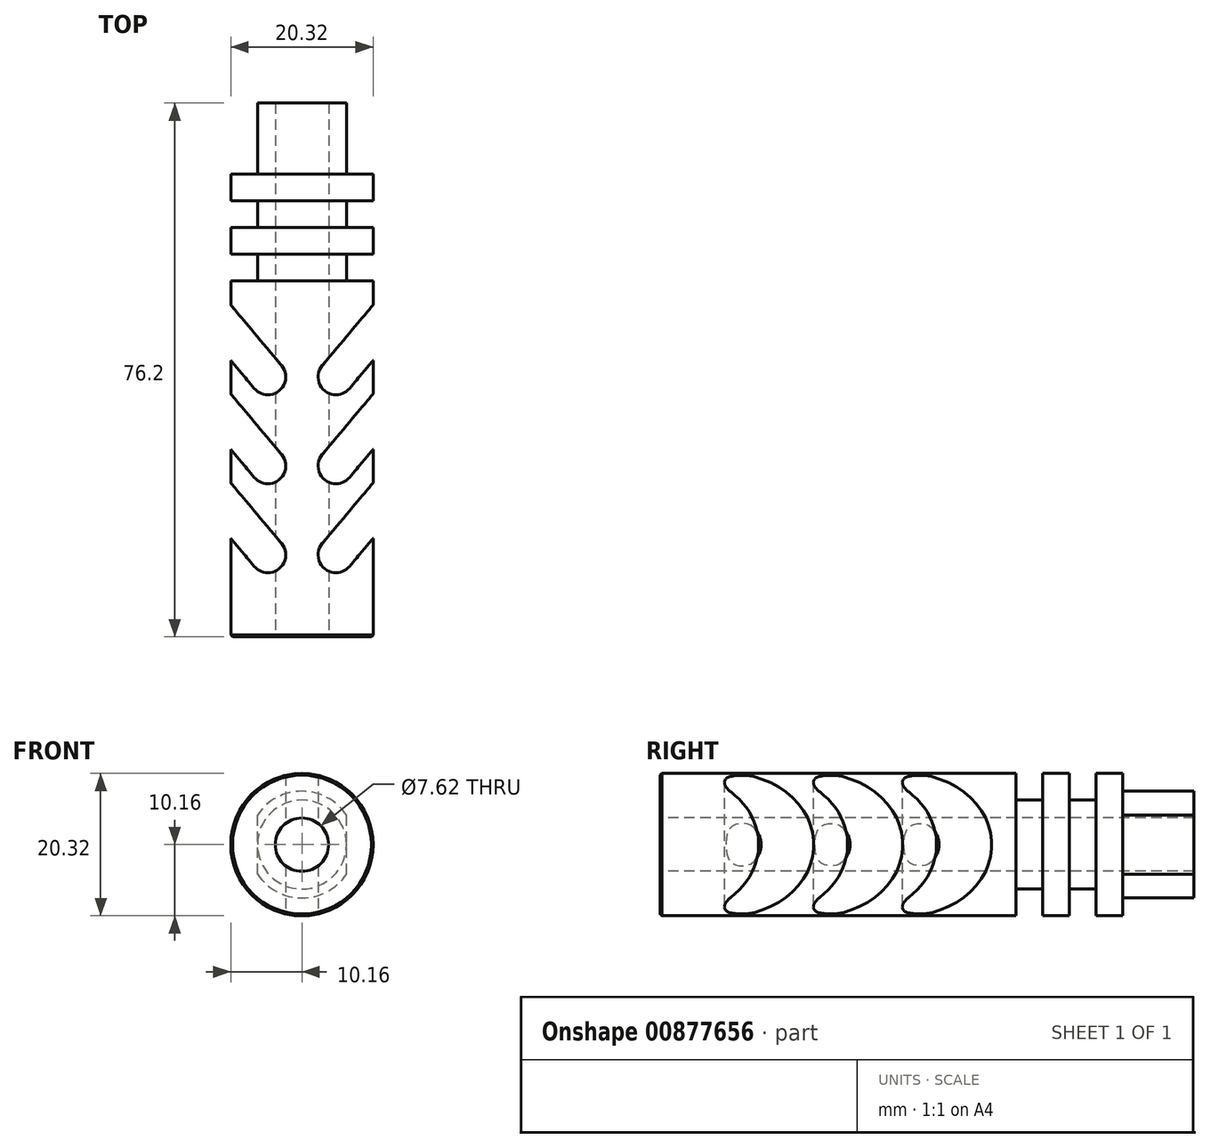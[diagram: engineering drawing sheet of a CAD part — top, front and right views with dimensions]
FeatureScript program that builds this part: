
annotation { "Feature Type Name" : "Feature", "Feature Type Description" : "" }
export const myFeature = defineFeature(function(context is Context, id is Id, definition is map)
    precondition{}
    {
        {
            var Q0;
            Q0=qCreatedBy(makeId("Front.planeOp"),FACE);
            var sketch = newSketch(context, id + "F0", { "sketchPlane" : qUnion([Q0])});
            skCircle(sketch, "E0", {"center": v(0, 0) * mm, "radius": 10.16 * mm});
            skSolve(sketch);
        }
        {
            var Q0;
            Q0=makeQuery(id+"F0.imprint","IMPRINT",FACE,{"disambiguationData":[TD([[makeQuery(id+"F0.imprint","IMPRINT",EDGE,{"derivedFrom":sQuery(id+"F0.wireOp",EDGE,"E0")}),1.0]])]});
            extrude(context, id + "F1", {"entities" : qUnion([Q0]), "oppositeDirection" : true, "depth" : 50.8 * mm, "offsetDistance" : 25.4 * mm});
        }
        {
            var Q0;
            Q0=makeQuery(id+"F1.opExtrude","CAP_FACE",FACE,{"disambiguationData":[OSD([sQuery(id+"F0.wireOp",EDGE,"E0")])],"isStart":false});
            var sketch = newSketch(context, id + "F2", { "sketchPlane" : qUnion([Q0])});
            skCircle(sketch, "E1", {"center": v(0, 0) * mm, "radius": 6.35 * mm});
            skSolve(sketch);
        }
        {
            var Q0;
            Q0=makeQuery(id+"F2.imprint","IMPRINT",FACE,{"disambiguationData":[TD([[makeQuery(id+"F2.imprint","IMPRINT",EDGE,{"derivedFrom":sQuery(id+"F2.wireOp",EDGE,"E1")}),1.0]])]});
            extrude(context, id + "F3", {"entities" : qUnion([Q0]), "operationType" : NewBodyOperationType.ADD, "depth" : 3.8 * mm, "offsetDistance" : 25.4 * mm});
        }
        {
            var Q0;
            Q0=makeQuery(id+"F3.opExtrude","CAP_FACE",FACE,{"disambiguationData":[OSD([sQuery(id+"F2.wireOp",EDGE,"E1")])],"isStart":false});
            var sketch = newSketch(context, id + "F4", { "sketchPlane" : qUnion([Q0])});
            skCircle(sketch, "E2", {"center": v(0, 0) * mm, "radius": 10.16 * mm});
            skSolve(sketch);
        }
        {
            var Q0;
            Q0 = qSketchRegion(id + "F4", true);
            extrude(context, id + "F5", {"entities" : qUnion([Q0]), "operationType" : NewBodyOperationType.ADD, "depth" : 3.8 * mm, "offsetDistance" : 25.4 * mm});
        }
        {
            var Q0;
            Q0=makeQuery(id+"F5.opExtrude","CAP_FACE",FACE,{"disambiguationData":[OSD([sQuery(id+"F4.wireOp",EDGE,"E2")])],"isStart":false});
            var sketch = newSketch(context, id + "F6", { "sketchPlane" : qUnion([Q0])});
            skCircle(sketch, "E3", {"center": v(0, 0) * mm, "radius": 6.35 * mm});
            skSolve(sketch);
        }
        {
            var Q0;
            Q0=makeQuery(id+"F6.imprint","IMPRINT",FACE,{"disambiguationData":[TD([[makeQuery(id+"F6.imprint","IMPRINT",EDGE,{"derivedFrom":sQuery(id+"F6.wireOp",EDGE,"E3")}),1.0]])]});
            extrude(context, id + "F7", {"entities" : qUnion([Q0]), "operationType" : NewBodyOperationType.ADD, "depth" : 3.8 * mm, "offsetDistance" : 25.4 * mm});
        }
        {
            var Q0;
            Q0=makeQuery(id+"F7.opExtrude","CAP_FACE",FACE,{"disambiguationData":[OSD([sQuery(id+"F6.wireOp",EDGE,"E3")])],"isStart":false});
            var sketch = newSketch(context, id + "F8", { "sketchPlane" : qUnion([Q0])});
            skCircle(sketch, "E4", {"center": v(0, 0) * mm, "radius": 10.16 * mm});
            skSolve(sketch);
        }
        {
            var Q0;
            Q0=makeQuery(id+"F8.imprint","IMPRINT",FACE,{"disambiguationData":[TD([[makeQuery(id+"F8.imprint","IMPRINT",EDGE,{"derivedFrom":makeQuery(id+"F7.opExtrude","CAP_EDGE",EDGE,{"disambiguationData":[OSD([sQuery(id+"F6.wireOp",EDGE,"E3")])],"isStart":false})}),1.0]])]});
            var Q1;
            Q1=makeQuery(id+"F8.imprint","IMPRINT",FACE,{"disambiguationData":[TD([[makeQuery(id+"F8.imprint","IMPRINT",EDGE,{"derivedFrom":sQuery(id+"F8.wireOp",EDGE,"E4")}),1.0]])]});
            extrude(context, id + "F9", {"entities" : qUnion([Q0, Q1]), "operationType" : NewBodyOperationType.ADD, "depth" : 3.8 * mm, "offsetDistance" : 25.4 * mm});
        }
        {
            var Q0;
            Q0=makeQuery(id+"F9.opExtrude","CAP_FACE",FACE,{"disambiguationData":[OSD([sQuery(id+"F8.wireOp",EDGE,"E4")])],"isStart":false});
            var sketch = newSketch(context, id + "F10", { "sketchPlane" : qUnion([Q0])});
            skCircle(sketch, "E5", {"center": v(0, 0) * mm, "radius": 7.62 * mm});
            skLineSegment(sketch, "E6", {"start": v(-6.35, -4.21) * mm, "end": v(-6.35, 4.21) * mm});
            skLineSegment(sketch, "E7.MirrorCS", {"start": v(6.35, -4.21) * mm, "end": v(6.35, 4.21) * mm});
            skSolve(sketch);
        }
        {
            var Q0;
            {var subQ0=sQuery(id+"F10.wireOp",EDGE,"E6");Q0=makeQuery(id+"F10.imprint","IMPRINT",FACE,{"disambiguationData":[TD([[makeQuery(id+"F10.imprint","IMPRINT",EDGE,{"derivedFrom":subQ0}),-1.0]])]});}
            var Q1;
            {var subQ0=sQuery(id+"F10.wireOp",EDGE,"E6");Q1=makeQuery(id+"F10.imprint","IMPRINT",FACE,{"disambiguationData":[TD([[makeQuery(id+"F10.imprint","IMPRINT",EDGE,{"derivedFrom":subQ0}),-1.0]])]});}
            extrude(context, id + "F11", {"entities" : qUnion([Q0, Q1]), "operationType" : NewBodyOperationType.ADD, "depth" : 10.16 * mm, "offsetDistance" : 25.4 * mm});
        }
        {
            var Q0;
            Q0=sQuery(id+"F0.wireOp",VERTEX,"E0.center");
            var Q1;
            Q1=makeQuery(id+"F1.opExtrude","SWEPT_BODY",BODY,{"disambiguationData":[OSD([sQuery(id+"F0.wireOp",EDGE,"E0")])]});
            hole(context, id + "F12", {"style" : HoleStyle.SIMPLE, "endStyle" : HoleEndStyle.THROUGH, "holeDiameter" : 7.62 * mm, "majorDiameter" : 6.35 * mm, "isTappedThrough" : true, "tappedDepth" : 12.7 * mm, "tapClearance" : 3, "startFromSketch" : true, "locations" : qUnion([Q0]), "scope" : qUnion([Q1])});
        }
        {
            var Q0;
            Q0=qCreatedBy(makeId("Top.planeOp"),FACE);
            var sketch = newSketch(context, id + "F13", { "sketchPlane" : qUnion([Q0])});
            skLineSegment(sketch, "E8", {"start": v(10.16, 0) * mm, "end": v(10.16, 50.8) * mm});
            skLineSegment(sketch, "E9", {"start": v(-10.16, 50.8) * mm, "end": v(-10.16, 0) * mm});
            skLineSegment(sketch, "E10", {"start": v(-15.47, 49.74) * mm, "end": v(-4.85, 37.1) * mm});
            skPoint(sketch, "E11", {"position": v(-10.16, 43.42) * mm});
            skArc(sketch, "E12.0.startCap", {"start": v(-17.41, 48.11) * mm, "mid": v(-17.1, 51.7) * mm, "end": v(-13.52, 51.38) * mm});
            skArc(sketch, "E12.0.endCap", {"start": v(-2.9, 38.73) * mm, "mid": v(-3.22, 35.15) * mm, "end": v(-6.8, 35.46) * mm});
            skLineSegment(sketch, "E12.0.left", {"start": v(-13.52, 51.38) * mm, "end": v(-2.9, 38.73) * mm});
            skLineSegment(sketch, "E12.0.right", {"start": v(-17.41, 48.11) * mm, "end": v(-6.8, 35.46) * mm});
            skArc(sketch, "E13.MirrorCS", {"start": v(2.9, 38.73) * mm, "mid": v(3.22, 35.15) * mm, "end": v(6.8, 35.46) * mm});
            skLineSegment(sketch, "E14.MirrorCS", {"start": v(10.16, 50.8) * mm, "end": v(10.16, 0) * mm});
            skLineSegment(sketch, "E15.MirrorCS", {"start": v(15.47, 49.74) * mm, "end": v(4.85, 37.1) * mm});
            skLineSegment(sketch, "E16.MirrorCS", {"start": v(17.41, 48.11) * mm, "end": v(6.8, 35.46) * mm});
            skPoint(sketch, "E17.MirrorP", {"position": v(10.16, 43.42) * mm});
            skArc(sketch, "E18.MirrorCS", {"start": v(17.41, 48.11) * mm, "mid": v(17.1, 51.7) * mm, "end": v(13.52, 51.38) * mm});
            skLineSegment(sketch, "E19.MirrorCS", {"start": v(13.52, 51.38) * mm, "end": v(2.9, 38.73) * mm});
            skArc(sketch, "E20.0.1.0", {"start": v(-17.41, 35.41) * mm, "mid": v(-17.1, 39) * mm, "end": v(-13.52, 38.68) * mm});
            skLineSegment(sketch, "E20.0.1.1", {"start": v(-13.52, 38.68) * mm, "end": v(-2.9, 26.03) * mm});
            skLineSegment(sketch, "E20.0.1.2", {"start": v(-15.47, 37.04) * mm, "end": v(-4.85, 24.4) * mm});
            skLineSegment(sketch, "E20.0.1.3", {"start": v(-17.41, 35.41) * mm, "end": v(-6.8, 22.76) * mm});
            skArc(sketch, "E20.0.1.4", {"start": v(-2.9, 26.03) * mm, "mid": v(-3.22, 22.45) * mm, "end": v(-6.8, 22.76) * mm});
            skArc(sketch, "E20.0.1.5", {"start": v(2.9, 26.03) * mm, "mid": v(3.22, 22.45) * mm, "end": v(6.8, 22.76) * mm});
            skLineSegment(sketch, "E20.0.1.6", {"start": v(13.52, 38.68) * mm, "end": v(2.9, 26.03) * mm});
            skLineSegment(sketch, "E20.0.1.7", {"start": v(17.41, 35.41) * mm, "end": v(6.8, 22.76) * mm});
            skArc(sketch, "E20.0.2.0", {"start": v(-17.41, 22.71) * mm, "mid": v(-17.1, 26.3) * mm, "end": v(-13.52, 25.98) * mm});
            skLineSegment(sketch, "E20.0.2.1", {"start": v(-13.52, 25.98) * mm, "end": v(-2.9, 13.33) * mm});
            skLineSegment(sketch, "E20.0.2.2", {"start": v(-15.47, 24.34) * mm, "end": v(-4.85, 11.7) * mm});
            skLineSegment(sketch, "E20.0.2.3", {"start": v(-17.41, 22.71) * mm, "end": v(-6.8, 10.06) * mm});
            skArc(sketch, "E20.0.2.4", {"start": v(-2.9, 13.33) * mm, "mid": v(-3.22, 9.75) * mm, "end": v(-6.8, 10.06) * mm});
            skArc(sketch, "E20.0.2.5", {"start": v(2.9, 13.33) * mm, "mid": v(3.22, 9.75) * mm, "end": v(6.8, 10.06) * mm});
            skLineSegment(sketch, "E20.0.2.6", {"start": v(13.52, 25.98) * mm, "end": v(2.9, 13.33) * mm});
            skLineSegment(sketch, "E20.0.2.7", {"start": v(17.41, 22.71) * mm, "end": v(6.8, 10.06) * mm});
            skLineSegment(sketch, "E20.direction1", {"start": v(-17.41, 48.11) * mm, "end": v(7.17, 48.11) * mm, "construction": true});
            skLineSegment(sketch, "E20.direction2", {"start": v(-17.41, 48.11) * mm, "end": v(-17.41, 35.41) * mm, "construction": true});
            skSolve(sketch);
        }
        {
            var Q0;
            Q0 = qSketchRegion(id + "F13", true);
            extrude(context, id + "F14", {"entities" : qUnion([Q0]), "operationType" : NewBodyOperationType.REMOVE, "endBound" : BoundingType.SYMMETRIC, "depth" : 25.4 * mm, "offsetDistance" : 25.4 * mm});
        }
        {
            var Q0;
            Q0=makeQuery(id+"F1.opExtrude","CAP_EDGE",EDGE,{"disambiguationData":[OSD([sQuery(id+"F0.wireOp",EDGE,"E0")])],"isStart":true});
            var Q1;
            Q1=makeQuery(id+"F12.hole-0.boolean.opBoolean","COPY",EDGE,{"derivedFrom":makeQuery(id+"F12.hole-0.opRevolve","SWEPT_EDGE",EDGE,{"disambiguationData":[OSD([sQuery(id+"F12.hole-0.sketch.wireOp",EDGE,"core_line_2"),sQuery(id+"F12.hole-0.sketch.wireOp",EDGE,"core_line_3")])]})});
            chamfer(context, id + "F15", {"entities" : qUnion([Q0, Q1]), "width" : 0.25 * mm, "tangentPropagation" : true});
        }
    });
